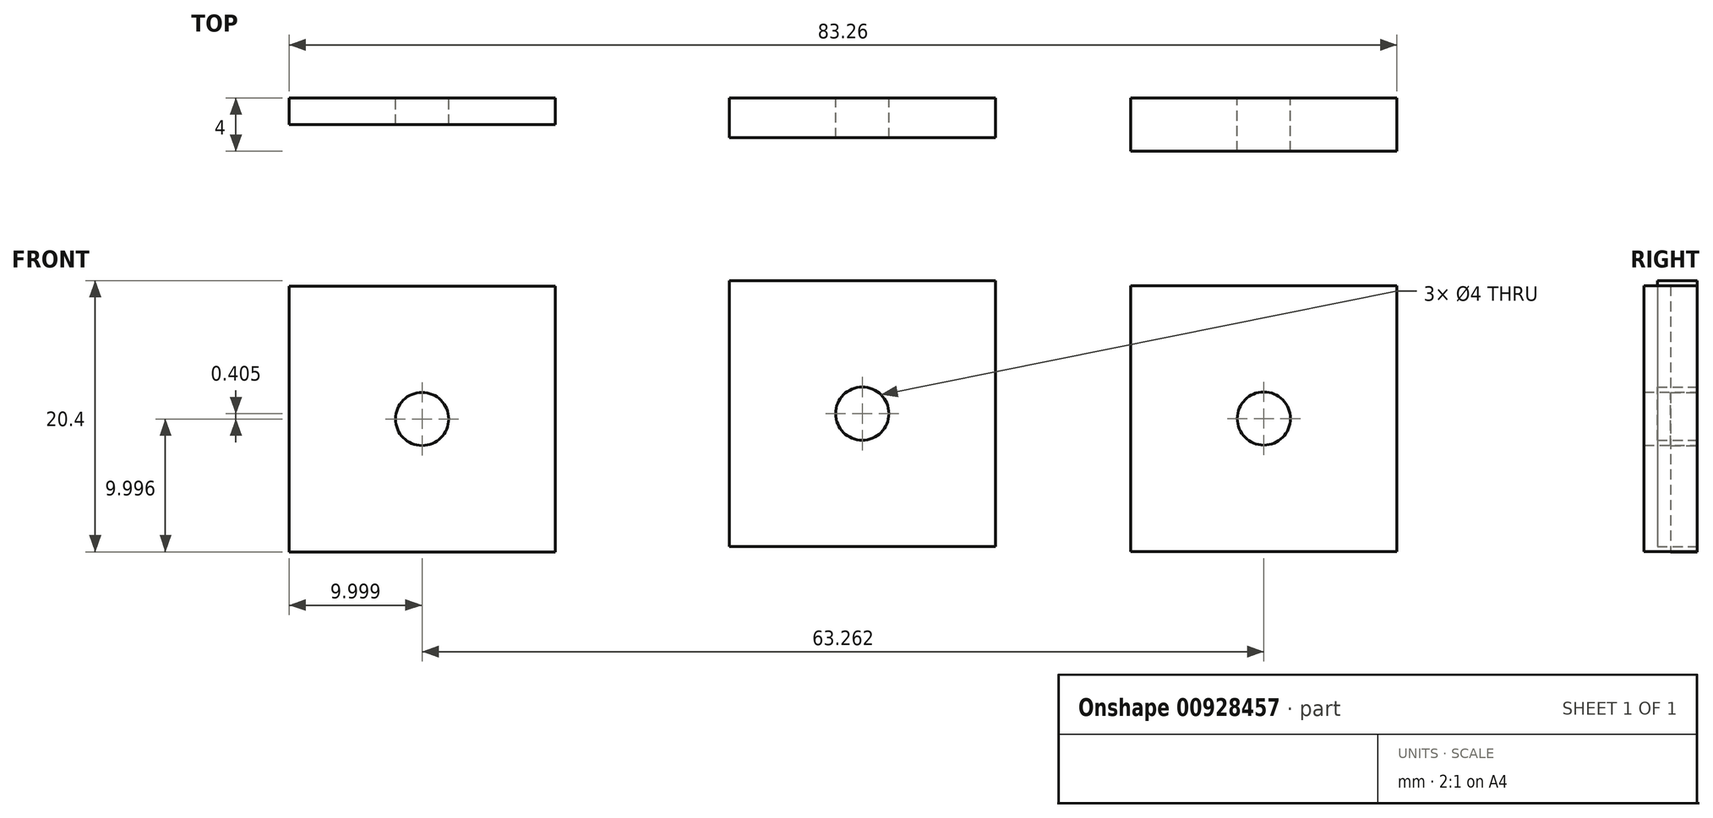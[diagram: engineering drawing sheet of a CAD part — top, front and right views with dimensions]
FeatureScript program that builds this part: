
annotation { "Feature Type Name" : "Feature", "Feature Type Description" : "" }
export const myFeature = defineFeature(function(context is Context, id is Id, definition is map)
    precondition{}
    {
        {
            var Q0;
            Q0=qCreatedBy(makeId("Front.planeOp"),FACE);
            var sketch = newSketch(context, id + "F0", { "sketchPlane" : qUnion([Q0])});
            skLineSegment(sketch, "E0.bottom", {"start": v(-45.4, 14.62) * mm, "end": v(-25.4, 14.62) * mm});
            skLineSegment(sketch, "E0.top", {"start": v(-45.4, -5.38) * mm, "end": v(-25.4, -5.38) * mm});
            skLineSegment(sketch, "E0.left", {"start": v(-45.4, 14.62) * mm, "end": v(-45.4, -5.38) * mm});
            skLineSegment(sketch, "E0.right", {"start": v(-25.4, 14.62) * mm, "end": v(-25.4, -5.38) * mm});
            skCircle(sketch, "E1", {"center": v(-35.4, 4.62) * mm, "radius": 2 * mm});
            skLineSegment(sketch, "E2", {"start": v(-35.4, 4.62) * mm, "end": v(43.25, 4.62) * mm, "construction": true});
            skLineSegment(sketch, "E3.bottom", {"start": v(-12.31, 15.02) * mm, "end": v(7.69, 15.02) * mm});
            skLineSegment(sketch, "E3.top", {"start": v(-12.31, -4.98) * mm, "end": v(7.69, -4.98) * mm});
            skLineSegment(sketch, "E3.left", {"start": v(-12.31, 15.02) * mm, "end": v(-12.31, -4.98) * mm});
            skLineSegment(sketch, "E3.right", {"start": v(7.69, 15.02) * mm, "end": v(7.69, -4.98) * mm});
            skCircle(sketch, "E4", {"center": v(-2.31, 5.02) * mm, "radius": 2 * mm});
            skLineSegment(sketch, "E5.bottom", {"start": v(17.87, 14.65) * mm, "end": v(37.87, 14.65) * mm});
            skLineSegment(sketch, "E5.top", {"start": v(17.87, -5.35) * mm, "end": v(37.87, -5.35) * mm});
            skLineSegment(sketch, "E5.left", {"start": v(17.87, 14.65) * mm, "end": v(17.87, -5.35) * mm});
            skLineSegment(sketch, "E5.right", {"start": v(37.87, 14.65) * mm, "end": v(37.87, -5.35) * mm});
            skCircle(sketch, "E6", {"center": v(27.87, 4.65) * mm, "radius": 2 * mm});
            skSolve(sketch);
        }
        {
            var Q0;
            Q0=makeQuery(id+"F0.imprint","IMPRINT",FACE,{"disambiguationData":[TD([[makeQuery(id+"F0.imprint","IMPRINT",EDGE,{"derivedFrom":sQuery(id+"F0.wireOp",EDGE,"E0.bottom")}),-1.0]])]});
            extrude(context, id + "F1", {"entities" : qUnion([Q0]), "depth" : 2 * mm, "offsetDistance" : 25 * mm});
        }
        {
            var Q0;
            Q0=makeQuery(id+"F0.imprint","IMPRINT",FACE,{"disambiguationData":[TD([[makeQuery(id+"F0.imprint","IMPRINT",EDGE,{"derivedFrom":sQuery(id+"F0.wireOp",EDGE,"E3.bottom")}),-1.0]])]});
            extrude(context, id + "F2", {"entities" : qUnion([Q0]), "depth" : 3 * mm, "offsetDistance" : 25 * mm});
        }
        {
            var Q0;
            Q0=makeQuery(id+"F0.imprint","IMPRINT",FACE,{"disambiguationData":[TD([[makeQuery(id+"F0.imprint","IMPRINT",EDGE,{"derivedFrom":sQuery(id+"F0.wireOp",EDGE,"E5.bottom")}),-1.0]])]});
            extrude(context, id + "F3", {"entities" : qUnion([Q0]), "depth" : 4 * mm, "offsetDistance" : 25 * mm});
        }
    });
